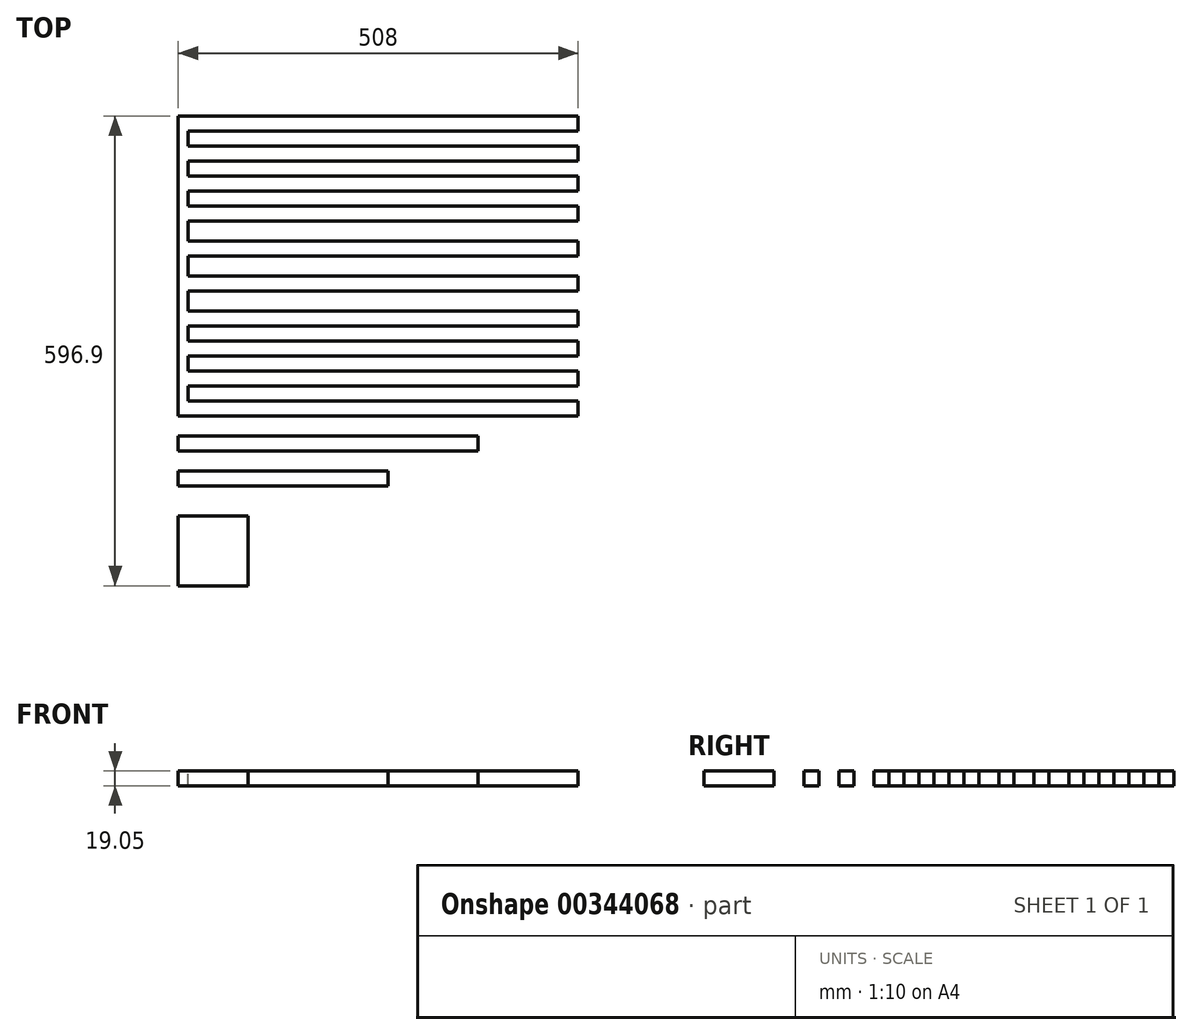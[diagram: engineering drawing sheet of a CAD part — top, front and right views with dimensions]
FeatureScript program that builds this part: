
annotation { "Feature Type Name" : "Feature", "Feature Type Description" : "" }
export const myFeature = defineFeature(function(context is Context, id is Id, definition is map)
    precondition{}
    {
        {
            var Q0;
            Q0=qCreatedBy(makeId("Top.planeOp"),FACE);
            var sketch = newSketch(context, id + "F0", { "sketchPlane" : qUnion([Q0])});
            skLineSegment(sketch, "E0.bottom", {"start": v(0, 0) * mm, "end": v(508, 0) * mm});
            skLineSegment(sketch, "E0.top", {"start": v(0, 381) * mm, "end": v(508, 381) * mm});
            skLineSegment(sketch, "E0.left", {"start": v(0, 0) * mm, "end": v(0, 381) * mm});
            skLineSegment(sketch, "E0.right", {"start": v(508, 0) * mm, "end": v(508, 381) * mm});
            skLineSegment(sketch, "E1", {"start": v(0, 361.95) * mm, "end": v(508, 361.95) * mm, "construction": true});
            skLineSegment(sketch, "E2", {"start": v(0, 342.9) * mm, "end": v(508, 342.9) * mm, "construction": true});
            skLineSegment(sketch, "E3", {"start": v(0, 323.85) * mm, "end": v(508, 323.85) * mm, "construction": true});
            skLineSegment(sketch, "E4", {"start": v(0, 304.8) * mm, "end": v(508, 304.8) * mm, "construction": true});
            skLineSegment(sketch, "E5", {"start": v(0, 285.75) * mm, "end": v(508, 285.75) * mm, "construction": true});
            skLineSegment(sketch, "E6", {"start": v(0, 266.7) * mm, "end": v(508, 266.7) * mm, "construction": true});
            skLineSegment(sketch, "E7", {"start": v(0, 247.65) * mm, "end": v(508, 247.65) * mm, "construction": true});
            skLineSegment(sketch, "E8", {"start": v(0, 222.25) * mm, "end": v(508, 222.25) * mm, "construction": true});
            skLineSegment(sketch, "E9", {"start": v(0, 203.2) * mm, "end": v(508, 203.2) * mm, "construction": true});
            skLineSegment(sketch, "E10", {"start": v(0, 177.8) * mm, "end": v(508, 177.8) * mm, "construction": true});
            skLineSegment(sketch, "E11", {"start": v(0, 158.75) * mm, "end": v(508, 158.75) * mm, "construction": true});
            skLineSegment(sketch, "E12", {"start": v(0, 133.35) * mm, "end": v(508, 133.35) * mm, "construction": true});
            skLineSegment(sketch, "E13", {"start": v(0, 114.3) * mm, "end": v(508, 114.3) * mm, "construction": true});
            skLineSegment(sketch, "E14", {"start": v(0, 95.25) * mm, "end": v(508, 95.25) * mm, "construction": true});
            skLineSegment(sketch, "E15", {"start": v(0, 76.2) * mm, "end": v(508, 76.2) * mm, "construction": true});
            skLineSegment(sketch, "E16", {"start": v(0, 57.15) * mm, "end": v(508, 57.15) * mm, "construction": true});
            skLineSegment(sketch, "E17", {"start": v(0, 38.1) * mm, "end": v(508, 38.1) * mm, "construction": true});
            skLineSegment(sketch, "E18", {"start": v(0, 19.05) * mm, "end": v(508, 19.05) * mm, "construction": true});
            skSolve(sketch);
        }
        {
            var Q0;
            {var subQ0=sQuery(id+"F0.wireOp",EDGE,"E0.top");Q0=makeQuery(id+"F0.imprint","IMPRINT",FACE,{"disambiguationData":[TD([[makeQuery(id+"F0.imprint","IMPRINT",EDGE,{"derivedFrom":subQ0}),-1.0]])]});}
            extrude(context, id + "F1", {"entities" : qUnion([Q0]), "depth" : 19.05 * mm});
        }
        {
            var Q0;
            Q0=makeQuery(id+"F1.opExtrude","CAP_FACE",FACE,{"disambiguationData":[OSD([sQuery(id+"F0.wireOp",EDGE,"E0.bottom"),sQuery(id+"F0.wireOp",EDGE,"E0.top"),sQuery(id+"F0.wireOp",EDGE,"E0.left"),sQuery(id+"F0.wireOp",EDGE,"E0.right")])],"isStart":false});
            var sketch = newSketch(context, id + "F2", { "sketchPlane" : qUnion([Q0])});
            skLineSegment(sketch, "E19.bottom", {"start": v(0, 361.95) * mm, "end": v(508, 361.95) * mm});
            skLineSegment(sketch, "E19.top", {"start": v(0, 342.9) * mm, "end": v(508, 342.9) * mm});
            skLineSegment(sketch, "E19.right", {"start": v(508, 361.95) * mm, "end": v(508, 342.9) * mm});
            skLineSegment(sketch, "E20", {"start": v(12.7, 361.95) * mm, "end": v(12.7, 342.9) * mm});
            skLineSegment(sketch, "E21", {"start": v(495.3, 361.95) * mm, "end": v(495.3, 342.9) * mm});
            skLineSegment(sketch, "E22.bottom", {"start": v(12.7, 323.85) * mm, "end": v(508, 323.85) * mm});
            skLineSegment(sketch, "E22.top", {"start": v(12.7, 304.8) * mm, "end": v(508, 304.8) * mm});
            skLineSegment(sketch, "E22.left", {"start": v(12.7, 323.85) * mm, "end": v(12.7, 304.8) * mm});
            skLineSegment(sketch, "E22.right", {"start": v(508, 323.85) * mm, "end": v(508, 304.8) * mm});
            skLineSegment(sketch, "E23.bottom", {"start": v(12.7, 285.75) * mm, "end": v(508, 285.75) * mm});
            skLineSegment(sketch, "E23.top", {"start": v(12.7, 266.7) * mm, "end": v(508, 266.7) * mm});
            skLineSegment(sketch, "E23.left", {"start": v(12.7, 285.75) * mm, "end": v(12.7, 266.7) * mm});
            skLineSegment(sketch, "E23.right", {"start": v(508, 285.75) * mm, "end": v(508, 266.7) * mm});
            skLineSegment(sketch, "E24.bottom", {"start": v(12.7, 247.65) * mm, "end": v(508, 247.65) * mm});
            skLineSegment(sketch, "E24.top", {"start": v(12.7, 222.25) * mm, "end": v(508, 222.25) * mm});
            skLineSegment(sketch, "E24.left", {"start": v(12.7, 247.65) * mm, "end": v(12.7, 222.25) * mm});
            skLineSegment(sketch, "E24.right", {"start": v(508, 247.65) * mm, "end": v(508, 222.25) * mm});
            skLineSegment(sketch, "E25.bottom", {"start": v(12.7, 203.2) * mm, "end": v(508, 203.2) * mm});
            skLineSegment(sketch, "E25.top", {"start": v(12.7, 177.8) * mm, "end": v(508, 177.8) * mm});
            skLineSegment(sketch, "E25.left", {"start": v(12.7, 203.2) * mm, "end": v(12.7, 177.8) * mm});
            skLineSegment(sketch, "E25.right", {"start": v(508, 203.2) * mm, "end": v(508, 177.8) * mm});
            skLineSegment(sketch, "E26.bottom", {"start": v(12.7, 158.75) * mm, "end": v(508, 158.75) * mm});
            skLineSegment(sketch, "E26.top", {"start": v(12.7, 133.35) * mm, "end": v(508, 133.35) * mm});
            skLineSegment(sketch, "E26.left", {"start": v(12.7, 158.75) * mm, "end": v(12.7, 133.35) * mm});
            skLineSegment(sketch, "E26.right", {"start": v(508, 158.75) * mm, "end": v(508, 133.35) * mm});
            skLineSegment(sketch, "E27.bottom", {"start": v(12.7, 114.3) * mm, "end": v(508, 114.3) * mm});
            skLineSegment(sketch, "E27.top", {"start": v(12.7, 95.25) * mm, "end": v(508, 95.25) * mm});
            skLineSegment(sketch, "E27.left", {"start": v(12.7, 114.3) * mm, "end": v(12.7, 95.25) * mm});
            skLineSegment(sketch, "E27.right", {"start": v(508, 114.3) * mm, "end": v(508, 95.25) * mm});
            skLineSegment(sketch, "E28.bottom", {"start": v(12.7, 76.2) * mm, "end": v(508, 76.2) * mm});
            skLineSegment(sketch, "E28.top", {"start": v(12.7, 57.15) * mm, "end": v(508, 57.15) * mm});
            skLineSegment(sketch, "E28.left", {"start": v(12.7, 76.2) * mm, "end": v(12.7, 57.15) * mm});
            skLineSegment(sketch, "E28.right", {"start": v(508, 76.2) * mm, "end": v(508, 57.15) * mm});
            skLineSegment(sketch, "E29.bottom", {"start": v(12.7, 38.1) * mm, "end": v(508, 38.1) * mm});
            skLineSegment(sketch, "E29.top", {"start": v(12.7, 19.05) * mm, "end": v(508, 19.05) * mm});
            skLineSegment(sketch, "E29.left", {"start": v(12.7, 38.1) * mm, "end": v(12.7, 19.05) * mm});
            skLineSegment(sketch, "E29.right", {"start": v(508, 38.1) * mm, "end": v(508, 19.05) * mm});
            skLineSegment(sketch, "E30", {"start": v(12.7, 342.9) * mm, "end": v(12.7, 323.85) * mm});
            skLineSegment(sketch, "E31", {"start": v(12.7, 304.8) * mm, "end": v(12.7, 285.75) * mm});
            skLineSegment(sketch, "E32", {"start": v(12.7, 266.7) * mm, "end": v(12.7, 247.65) * mm});
            skLineSegment(sketch, "E33", {"start": v(12.7, 222.25) * mm, "end": v(12.7, 203.2) * mm});
            skLineSegment(sketch, "E34", {"start": v(12.7, 177.8) * mm, "end": v(12.7, 158.75) * mm});
            skLineSegment(sketch, "E35", {"start": v(12.7, 133.35) * mm, "end": v(12.7, 114.3) * mm});
            skLineSegment(sketch, "E36", {"start": v(12.7, 95.25) * mm, "end": v(12.7, 76.2) * mm});
            skLineSegment(sketch, "E37", {"start": v(12.7, 57.15) * mm, "end": v(12.7, 38.1) * mm});
            skSolve(sketch);
        }
        {
            var Q0;
            Q0 = qSketchRegion(id + "F2", true);
            extrude(context, id + "F3", {"entities" : qUnion([Q0]), "operationType" : NewBodyOperationType.REMOVE, "oppositeDirection" : true, "depth" : 25.4 * mm});
        }
        {
            var Q0;
            Q0=qCreatedBy(makeId("Top.planeOp"),FACE);
            var sketch = newSketch(context, id + "F4", { "sketchPlane" : qUnion([Q0])});
            skLineSegment(sketch, "E38.bottom", {"start": v(0, -25.4) * mm, "end": v(381, -25.4) * mm});
            skLineSegment(sketch, "E38.top", {"start": v(0, -44.45) * mm, "end": v(381, -44.45) * mm});
            skLineSegment(sketch, "E38.left", {"start": v(0, -25.4) * mm, "end": v(0, -44.45) * mm});
            skLineSegment(sketch, "E38.right", {"start": v(381, -25.4) * mm, "end": v(381, -44.45) * mm});
            skLineSegment(sketch, "E39.bottom", {"start": v(0, -69.85) * mm, "end": v(266.7, -69.85) * mm});
            skLineSegment(sketch, "E39.top", {"start": v(0, -88.9) * mm, "end": v(266.7, -88.9) * mm});
            skLineSegment(sketch, "E39.left", {"start": v(0, -69.85) * mm, "end": v(0, -88.9) * mm});
            skLineSegment(sketch, "E39.right", {"start": v(266.7, -69.85) * mm, "end": v(266.7, -88.9) * mm});
            skLineSegment(sketch, "E40.bottom", {"start": v(0, -127) * mm, "end": v(88.9, -127) * mm});
            skLineSegment(sketch, "E40.top", {"start": v(0, -215.9) * mm, "end": v(88.9, -215.9) * mm});
            skLineSegment(sketch, "E40.left", {"start": v(0, -127) * mm, "end": v(0, -215.9) * mm});
            skLineSegment(sketch, "E40.right", {"start": v(88.9, -127) * mm, "end": v(88.9, -215.9) * mm});
            skSolve(sketch);
        }
        {
            var Q0;
            Q0=makeQuery(id+"F4.imprint","IMPRINT",FACE,{"disambiguationData":[TD([[makeQuery(id+"F4.imprint","IMPRINT",EDGE,{"derivedFrom":sQuery(id+"F4.wireOp",EDGE,"E38.bottom")}),-1.0]])]});
            var Q1;
            Q1=makeQuery(id+"F4.imprint","IMPRINT",FACE,{"disambiguationData":[TD([[makeQuery(id+"F4.imprint","IMPRINT",EDGE,{"derivedFrom":sQuery(id+"F4.wireOp",EDGE,"E39.bottom")}),-1.0]])]});
            var Q2;
            Q2=makeQuery(id+"F4.imprint","IMPRINT",FACE,{"disambiguationData":[TD([[makeQuery(id+"F4.imprint","IMPRINT",EDGE,{"derivedFrom":sQuery(id+"F4.wireOp",EDGE,"E40.bottom")}),-1.0]])]});
            extrude(context, id + "F5", {"entities" : qUnion([Q0, Q1, Q2]), "depth" : 19.05 * mm});
        }
    });
